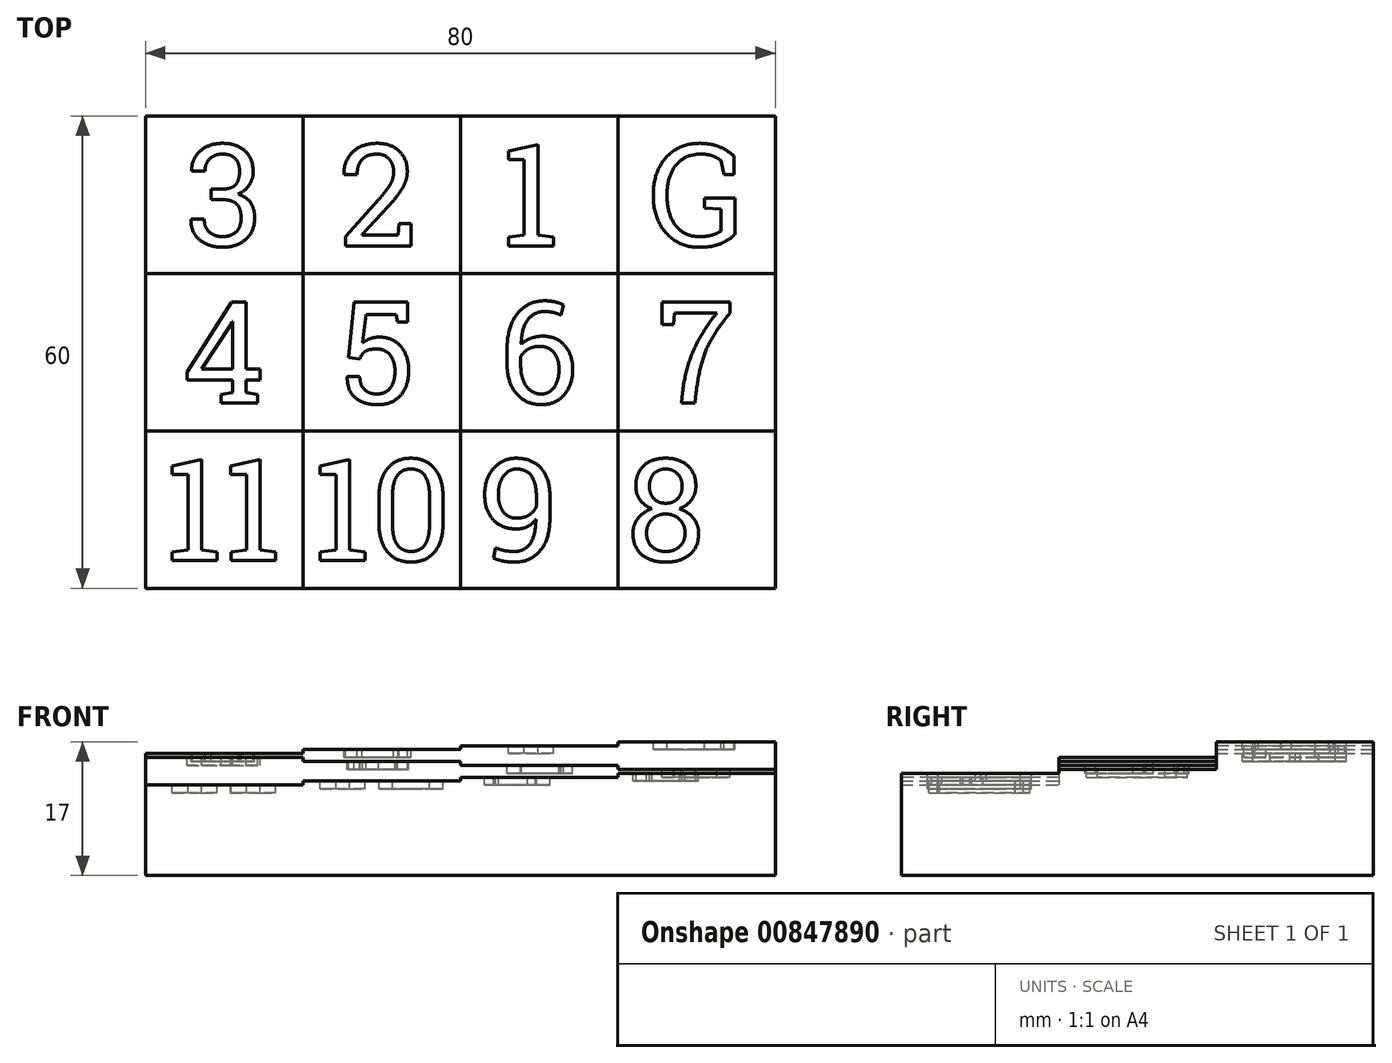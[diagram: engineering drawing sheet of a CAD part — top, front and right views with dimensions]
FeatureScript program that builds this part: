
annotation { "Feature Type Name" : "Feature", "Feature Type Description" : "" }
export const myFeature = defineFeature(function(context is Context, id is Id, definition is map)
    precondition{}
    {
        {
            var Q0;
            Q0=qCreatedBy(makeId("Top.planeOp"),FACE);
            var sketch = newSketch(context, id + "F0", { "sketchPlane" : qUnion([Q0])});
            skLineSegment(sketch, "E0.bottom", {"start": v(0, 0) * mm, "end": v(80, 0) * mm});
            skLineSegment(sketch, "E0.top", {"start": v(0, 60) * mm, "end": v(80, 60) * mm});
            skLineSegment(sketch, "E0.left", {"start": v(0, 0) * mm, "end": v(0, 60) * mm});
            skLineSegment(sketch, "E0.right", {"start": v(80, 0) * mm, "end": v(80, 60) * mm});
            skLineSegment(sketch, "E1", {"start": v(20, 0) * mm, "end": v(20, 60) * mm});
            skLineSegment(sketch, "E2", {"start": v(40, 60) * mm, "end": v(40, 0) * mm});
            skLineSegment(sketch, "E3", {"start": v(60, 60) * mm, "end": v(60, 0) * mm});
            skLineSegment(sketch, "E4", {"start": v(0, 40) * mm, "end": v(80, 40) * mm});
            skLineSegment(sketch, "E5", {"start": v(0, 20) * mm, "end": v(80, 20) * mm});
            skSolve(sketch);
        }
        {
            assignVariable(context, id + "F1", {"variableType" : VariableType.LENGTH, "name" : "H", "lengthValue" : 17 * mm});
        }
        {
            var Q0;
            {var subQ0=sQuery(id+"F0.wireOp",EDGE,"E0.right");var subQ1=sQuery(id+"F0.wireOp",EDGE,"E0.top");var subQ2=makeQuery(id+"F0.imprint","INTERSECT",VERTEX,{"derivedFrom":[subQ1,subQ0]});Q0=makeQuery(id+"F0.imprint","IMPRINT",FACE,{"disambiguationData":[TD([[makeQuery(id+"F0.imprint","IMPRINT",EDGE,{"disambiguationData":[TD([[subQ2,1.0]])],"derivedFrom":subQ1}),-1.0]])]});}
            extrude(context, id + "F2", {"entities" : qUnion([Q0]), "depth" : getVariable(context, 'H'), "offsetDistance" : 25 * mm});
        }
        {
            var Q0;
            {var subQ0=sQuery(id+"F0.wireOp",EDGE,"E2");var subQ1=sQuery(id+"F0.wireOp",EDGE,"E0.top");var subQ2=makeQuery(id+"F0.imprint","INTERSECT",VERTEX,{"derivedFrom":[subQ1,subQ0]});Q0=makeQuery(id+"F0.imprint","IMPRINT",FACE,{"disambiguationData":[TD([[makeQuery(id+"F0.imprint","IMPRINT",EDGE,{"disambiguationData":[TD([[subQ2,-1.0]])],"derivedFrom":subQ1}),-1.0]])]});}
            extrude(context, id + "F3", {"entities" : qUnion([Q0]), "operationType" : NewBodyOperationType.ADD, "depth" : (getVariable(context, 'H')) - 0.5 * mm, "offsetDistance" : 25 * mm});
        }
        {
            var Q0;
            {var subQ0=sQuery(id+"F0.wireOp",EDGE,"E1");var subQ1=sQuery(id+"F0.wireOp",EDGE,"E0.top");var subQ2=makeQuery(id+"F0.imprint","INTERSECT",VERTEX,{"derivedFrom":[subQ1,subQ0]});Q0=makeQuery(id+"F0.imprint","IMPRINT",FACE,{"disambiguationData":[TD([[makeQuery(id+"F0.imprint","IMPRINT",EDGE,{"disambiguationData":[TD([[subQ2,-1.0]])],"derivedFrom":subQ1}),-1.0]])]});}
            extrude(context, id + "F4", {"entities" : qUnion([Q0]), "operationType" : NewBodyOperationType.ADD, "depth" : (getVariable(context, 'H')) - 1 * mm, "offsetDistance" : 25 * mm});
        }
        {
            var Q0;
            {var subQ0=sQuery(id+"F0.wireOp",EDGE,"E0.left");var subQ1=sQuery(id+"F0.wireOp",EDGE,"E0.top");var subQ2=makeQuery(id+"F0.imprint","INTERSECT",VERTEX,{"derivedFrom":[subQ1,subQ0]});Q0=makeQuery(id+"F0.imprint","IMPRINT",FACE,{"disambiguationData":[TD([[makeQuery(id+"F0.imprint","IMPRINT",EDGE,{"disambiguationData":[TD([[subQ2,-1.0]])],"derivedFrom":subQ1}),-1.0]])]});}
            extrude(context, id + "F5", {"entities" : qUnion([Q0]), "operationType" : NewBodyOperationType.ADD, "depth" : (getVariable(context, 'H')) - 1.5 * mm, "offsetDistance" : 25 * mm});
        }
        {
            var Q0;
            {var subQ0=sQuery(id+"F0.wireOp",EDGE,"E4");var subQ1=sQuery(id+"F0.wireOp",EDGE,"E0.left");var subQ2=makeQuery(id+"F0.imprint","INTERSECT",VERTEX,{"derivedFrom":[subQ1,subQ0]});Q0=makeQuery(id+"F0.imprint","IMPRINT",FACE,{"disambiguationData":[TD([[makeQuery(id+"F0.imprint","IMPRINT",EDGE,{"disambiguationData":[TD([[subQ2,1.0]])],"derivedFrom":subQ1}),-1.0]])]});}
            extrude(context, id + "F6", {"entities" : qUnion([Q0]), "operationType" : NewBodyOperationType.ADD, "depth" : (getVariable(context, 'H')) - 2 * mm, "offsetDistance" : 25 * mm});
        }
        {
            var Q0;
            {var subQ0=sQuery(id+"F0.wireOp",EDGE,"E5");var subQ1=sQuery(id+"F0.wireOp",EDGE,"E1");var subQ2=makeQuery(id+"F0.imprint","INTERSECT",VERTEX,{"derivedFrom":[subQ1,subQ0]});Q0=makeQuery(id+"F0.imprint","IMPRINT",FACE,{"disambiguationData":[TD([[makeQuery(id+"F0.imprint","IMPRINT",EDGE,{"disambiguationData":[TD([[subQ2,-1.0]])],"derivedFrom":subQ1}),-1.0]])]});}
            extrude(context, id + "F7", {"entities" : qUnion([Q0]), "operationType" : NewBodyOperationType.ADD, "depth" : (getVariable(context, 'H')) - 2.5 * mm, "offsetDistance" : 25 * mm});
        }
        {
            var Q0;
            {var subQ0=sQuery(id+"F0.wireOp",EDGE,"E4");var subQ1=sQuery(id+"F0.wireOp",EDGE,"E2");var subQ2=makeQuery(id+"F0.imprint","INTERSECT",VERTEX,{"derivedFrom":[subQ1,subQ0]});Q0=makeQuery(id+"F0.imprint","IMPRINT",FACE,{"disambiguationData":[TD([[makeQuery(id+"F0.imprint","IMPRINT",EDGE,{"disambiguationData":[TD([[subQ2,-1.0]])],"derivedFrom":subQ1}),1.0]])]});}
            extrude(context, id + "F8", {"entities" : qUnion([Q0]), "operationType" : NewBodyOperationType.ADD, "depth" : (getVariable(context, 'H')) - 3 * mm, "offsetDistance" : 25 * mm});
        }
        {
            var Q0;
            {var subQ0=sQuery(id+"F0.wireOp",EDGE,"E4");var subQ1=sQuery(id+"F0.wireOp",EDGE,"E0.right");var subQ2=makeQuery(id+"F0.imprint","INTERSECT",VERTEX,{"derivedFrom":[subQ1,subQ0]});Q0=makeQuery(id+"F0.imprint","IMPRINT",FACE,{"disambiguationData":[TD([[makeQuery(id+"F0.imprint","IMPRINT",EDGE,{"disambiguationData":[TD([[subQ2,1.0]])],"derivedFrom":subQ1}),1.0]])]});}
            extrude(context, id + "F9", {"entities" : qUnion([Q0]), "operationType" : NewBodyOperationType.ADD, "depth" : (getVariable(context, 'H')) - 3.5 * mm, "offsetDistance" : 25 * mm});
        }
        {
            var Q0;
            {var subQ0=sQuery(id+"F0.wireOp",EDGE,"E2");var subQ1=sQuery(id+"F0.wireOp",EDGE,"E0.bottom");var subQ2=makeQuery(id+"F0.imprint","INTERSECT",VERTEX,{"derivedFrom":[subQ1,subQ0]});Q0=makeQuery(id+"F0.imprint","IMPRINT",FACE,{"disambiguationData":[TD([[makeQuery(id+"F0.imprint","IMPRINT",EDGE,{"disambiguationData":[TD([[subQ2,-1.0]])],"derivedFrom":subQ1}),1.0]])]});}
            extrude(context, id + "F10", {"entities" : qUnion([Q0]), "operationType" : NewBodyOperationType.ADD, "depth" : (getVariable(context, 'H')) - 4.5 * mm, "offsetDistance" : 25 * mm});
        }
        {
            var Q0;
            {var subQ0=sQuery(id+"F0.wireOp",EDGE,"E0.left");var subQ1=sQuery(id+"F0.wireOp",EDGE,"E0.bottom");var subQ2=makeQuery(id+"F0.imprint","INTERSECT",VERTEX,{"derivedFrom":[subQ1,subQ0]});Q0=makeQuery(id+"F0.imprint","IMPRINT",FACE,{"disambiguationData":[TD([[makeQuery(id+"F0.imprint","IMPRINT",EDGE,{"disambiguationData":[TD([[subQ2,-1.0]])],"derivedFrom":subQ1}),1.0]])]});}
            extrude(context, id + "F11", {"entities" : qUnion([Q0]), "operationType" : NewBodyOperationType.ADD, "depth" : (getVariable(context, 'H')) - 5.5 * mm, "offsetDistance" : 25 * mm});
        }
        {
            var Q0;
            {var subQ0=sQuery(id+"F0.wireOp",EDGE,"E0.right");var subQ1=sQuery(id+"F0.wireOp",EDGE,"E0.bottom");var subQ2=makeQuery(id+"F0.imprint","INTERSECT",VERTEX,{"derivedFrom":[subQ1,subQ0]});Q0=makeQuery(id+"F0.imprint","IMPRINT",FACE,{"disambiguationData":[TD([[makeQuery(id+"F0.imprint","IMPRINT",EDGE,{"disambiguationData":[TD([[subQ2,1.0]])],"derivedFrom":subQ1}),1.0]])]});}
            extrude(context, id + "F12", {"entities" : qUnion([Q0]), "operationType" : NewBodyOperationType.ADD, "depth" : (getVariable(context, 'H')) - 4 * mm, "offsetDistance" : 25 * mm});
        }
        {
            var Q0;
            {var subQ0=sQuery(id+"F0.wireOp",EDGE,"E1");var subQ1=sQuery(id+"F0.wireOp",EDGE,"E0.bottom");var subQ2=makeQuery(id+"F0.imprint","INTERSECT",VERTEX,{"derivedFrom":[subQ1,subQ0]});Q0=makeQuery(id+"F0.imprint","IMPRINT",FACE,{"disambiguationData":[TD([[makeQuery(id+"F0.imprint","IMPRINT",EDGE,{"disambiguationData":[TD([[subQ2,-1.0]])],"derivedFrom":subQ1}),1.0]])]});}
            extrude(context, id + "F13", {"entities" : qUnion([Q0]), "operationType" : NewBodyOperationType.ADD, "depth" : (getVariable(context, 'H')) - 5 * mm, "offsetDistance" : 25 * mm});
        }
        {
            var Q0;
            Q0=makeQuery(id+"F2.opExtrude","CAP_FACE",FACE,{"disambiguationData":[OSD([sQuery(id+"F0.wireOp",EDGE,"E0.top"),sQuery(id+"F0.wireOp",EDGE,"E0.right"),sQuery(id+"F0.wireOp",EDGE,"E3"),sQuery(id+"F0.wireOp",EDGE,"E4")])],"isStart":false});
            var sketch = newSketch(context, id + "F14", { "sketchPlane" : qUnion([Q0])});
            skText(sketch, "E6", { "text": "G", "fontName": "RobotoSlab-Regular.ttf"});
            skLineSegment(sketch, "E7", {"start": v(70, 40) * mm, "end": v(70, 43.5) * mm, "construction": true});
            skLineSegment(sketch, "E8", {"start": v(60, 50) * mm, "end": v(64.02, 50) * mm, "construction": true});
            const initialGuessF14  = {"E6": [0.06402, 0.0435, 1, 0, 0.013]};
            skSetInitialGuess(sketch, initialGuessF14);
            skSolve(sketch);
        }
        {
            var Q0;
            Q0=makeQuery(id+"F14.imprint","IMPRINT",FACE,{"disambiguationData":[TD([[makeQuery(id+"F14.imprint","IMPRINT",EDGE,{"derivedFrom":sQuery(id+"F14.wireOp",EDGE,"E6.sketch_text.stroke-0")}),-1.0]])]});
            extrude(context, id + "F15", {"entities" : qUnion([Q0]), "operationType" : NewBodyOperationType.REMOVE, "oppositeDirection" : true, "depth" : 1 * mm, "offsetDistance" : 25 * mm});
        }
        {
            var Q0;
            Q0=makeQuery(id+"F3.opExtrude","CAP_FACE",FACE,{"disambiguationData":[OSD([sQuery(id+"F0.wireOp",EDGE,"E0.top"),sQuery(id+"F0.wireOp",EDGE,"E2"),sQuery(id+"F0.wireOp",EDGE,"E3"),sQuery(id+"F0.wireOp",EDGE,"E4")])],"isStart":false});
            var sketch = newSketch(context, id + "F16", { "sketchPlane" : qUnion([Q0])});
            skText(sketch, "E9", { "text": "1", "fontName": "RobotoSlab-Regular.ttf"});
            skLineSegment(sketch, "E10", {"start": v(40, 50) * mm, "end": v(46.06, 50) * mm, "construction": true});
            skLineSegment(sketch, "E11", {"start": v(50, 40) * mm, "end": v(50, 43.5) * mm, "construction": true});
            const initialGuessF16  = {"E9": [0.04506, 0.0435, 1, 0, 0.013]};
            skSetInitialGuess(sketch, initialGuessF16);
            skSolve(sketch);
        }
        {
            var Q0;
            Q0 = qSketchRegion(id + "F16", true);
            extrude(context, id + "F17", {"entities" : qUnion([Q0]), "operationType" : NewBodyOperationType.REMOVE, "oppositeDirection" : true, "depth" : 1 * mm, "offsetDistance" : 25 * mm});
        }
        {
            var Q0;
            Q0=makeQuery(id+"F4.opExtrude","CAP_FACE",FACE,{"disambiguationData":[OSD([sQuery(id+"F0.wireOp",EDGE,"E0.top"),sQuery(id+"F0.wireOp",EDGE,"E1"),sQuery(id+"F0.wireOp",EDGE,"E2"),sQuery(id+"F0.wireOp",EDGE,"E4")])],"isStart":false});
            var sketch = newSketch(context, id + "F18", { "sketchPlane" : qUnion([Q0])});
            skText(sketch, "E12", { "text": "2", "fontName": "RobotoSlab-Regular.ttf"});
            skLineSegment(sketch, "E13", {"start": v(20, 50) * mm, "end": v(24.86, 50) * mm, "construction": true});
            skLineSegment(sketch, "E14", {"start": v(30, 43.5) * mm, "end": v(30, 40) * mm, "construction": true});
            const initialGuessF18  = {"E12": [0.02453, 0.0435, 1, 0, 0.013]};
            skSetInitialGuess(sketch, initialGuessF18);
            skSolve(sketch);
        }
        {
            var Q0;
            Q0 = qSketchRegion(id + "F18", true);
            extrude(context, id + "F19", {"entities" : qUnion([Q0]), "operationType" : NewBodyOperationType.REMOVE, "oppositeDirection" : true, "depth" : 1 * mm, "offsetDistance" : 25 * mm});
        }
        {
            var Q0;
            Q0=makeQuery(id+"F5.opExtrude","CAP_FACE",FACE,{"disambiguationData":[OSD([sQuery(id+"F0.wireOp",EDGE,"E0.top"),sQuery(id+"F0.wireOp",EDGE,"E0.left"),sQuery(id+"F0.wireOp",EDGE,"E1"),sQuery(id+"F0.wireOp",EDGE,"E4")])],"isStart":false});
            var sketch = newSketch(context, id + "F20", { "sketchPlane" : qUnion([Q0])});
            skText(sketch, "E15", { "text": "3", "fontName": "RobotoSlab-Regular.ttf"});
            skLineSegment(sketch, "E16", {"start": v(0, 50) * mm, "end": v(5.06, 50) * mm, "construction": true});
            skLineSegment(sketch, "E17", {"start": v(10, 43.5) * mm, "end": v(10, 40) * mm, "construction": true});
            const initialGuessF20  = {"E15": [0.00511, 0.0435, 1, 0, 0.013]};
            skSetInitialGuess(sketch, initialGuessF20);
            skSolve(sketch);
        }
        {
            var Q0;
            Q0 = qSketchRegion(id + "F20", true);
            extrude(context, id + "F21", {"entities" : qUnion([Q0]), "operationType" : NewBodyOperationType.REMOVE, "oppositeDirection" : true, "depth" : 1 * mm, "offsetDistance" : 25 * mm});
        }
        {
            var Q0;
            Q0=makeQuery(id+"F6.opExtrude","CAP_FACE",FACE,{"disambiguationData":[OSD([sQuery(id+"F0.wireOp",EDGE,"E0.left"),sQuery(id+"F0.wireOp",EDGE,"E1"),sQuery(id+"F0.wireOp",EDGE,"E4"),sQuery(id+"F0.wireOp",EDGE,"E5")])],"isStart":false});
            var sketch = newSketch(context, id + "F22", { "sketchPlane" : qUnion([Q0])});
            skText(sketch, "E18", { "text": "4", "fontName": "RobotoSlab-Regular.ttf"});
            skLineSegment(sketch, "E19", {"start": v(0, 30) * mm, "end": v(4.53, 30) * mm, "construction": true});
            skLineSegment(sketch, "E20", {"start": v(10, 23.5) * mm, "end": v(10, 20) * mm, "construction": true});
            const initialGuessF22  = {"E18": [0.00474, 0.0235, 1, 0, 0.013]};
            skSetInitialGuess(sketch, initialGuessF22);
            skSolve(sketch);
        }
        {
            var Q0;
            Q0 = qSketchRegion(id + "F22", true);
            extrude(context, id + "F23", {"entities" : qUnion([Q0]), "operationType" : NewBodyOperationType.REMOVE, "oppositeDirection" : true, "depth" : 1 * mm, "offsetDistance" : 25 * mm});
        }
        {
            var Q0;
            Q0=makeQuery(id+"F7.opExtrude","CAP_FACE",FACE,{"disambiguationData":[OSD([sQuery(id+"F0.wireOp",EDGE,"E1"),sQuery(id+"F0.wireOp",EDGE,"E2"),sQuery(id+"F0.wireOp",EDGE,"E4"),sQuery(id+"F0.wireOp",EDGE,"E5")])],"isStart":false});
            var sketch = newSketch(context, id + "F24", { "sketchPlane" : qUnion([Q0])});
            skText(sketch, "E21", { "text": "5", "fontName": "RobotoSlab-Regular.ttf"});
            skLineSegment(sketch, "E22", {"start": v(40, 30) * mm, "end": v(34.89, 30) * mm, "construction": true});
            skLineSegment(sketch, "E23", {"start": v(30, 23.5) * mm, "end": v(30, 20) * mm, "construction": true});
            const initialGuessF24  = {"E21": [0.02477, 0.0235, 1, 0, 0.013]};
            skSetInitialGuess(sketch, initialGuessF24);
            skSolve(sketch);
        }
        {
            var Q0;
            Q0 = qSketchRegion(id + "F24", true);
            extrude(context, id + "F25", {"entities" : qUnion([Q0]), "operationType" : NewBodyOperationType.REMOVE, "oppositeDirection" : true, "depth" : 1 * mm, "offsetDistance" : 25 * mm});
        }
        {
            var Q0;
            Q0=makeQuery(id+"F8.opExtrude","CAP_FACE",FACE,{"disambiguationData":[OSD([sQuery(id+"F0.wireOp",EDGE,"E2"),sQuery(id+"F0.wireOp",EDGE,"E3"),sQuery(id+"F0.wireOp",EDGE,"E4"),sQuery(id+"F0.wireOp",EDGE,"E5")])],"isStart":false});
            var sketch = newSketch(context, id + "F26", { "sketchPlane" : qUnion([Q0])});
            skText(sketch, "E24", { "text": "6", "fontName": "RobotoSlab-Regular.ttf"});
            skLineSegment(sketch, "E25", {"start": v(55.26, 30) * mm, "end": v(60, 30) * mm, "construction": true});
            skLineSegment(sketch, "E26", {"start": v(50, 23.5) * mm, "end": v(50, 20) * mm, "construction": true});
            const initialGuessF26  = {"E24": [0.04486, 0.0235, 1, 0, 0.013]};
            skSetInitialGuess(sketch, initialGuessF26);
            skSolve(sketch);
        }
        {
            var Q0;
            Q0 = qSketchRegion(id + "F26", true);
            extrude(context, id + "F27", {"entities" : qUnion([Q0]), "operationType" : NewBodyOperationType.REMOVE, "oppositeDirection" : true, "depth" : 1 * mm, "offsetDistance" : 25 * mm});
        }
        {
            var Q0;
            Q0=makeQuery(id+"F9.opExtrude","CAP_FACE",FACE,{"disambiguationData":[OSD([sQuery(id+"F0.wireOp",EDGE,"E0.right"),sQuery(id+"F0.wireOp",EDGE,"E3"),sQuery(id+"F0.wireOp",EDGE,"E4"),sQuery(id+"F0.wireOp",EDGE,"E5")])],"isStart":false});
            var sketch = newSketch(context, id + "F28", { "sketchPlane" : qUnion([Q0])});
            skText(sketch, "E27", { "text": "7", "fontName": "RobotoSlab-Regular.ttf"});
            skLineSegment(sketch, "E28", {"start": v(80, 30) * mm, "end": v(75.23, 30) * mm, "construction": true});
            skLineSegment(sketch, "E29", {"start": v(70, 23.5) * mm, "end": v(70, 20) * mm, "construction": true});
            const initialGuessF28  = {"E27": [0.06492, 0.0235, 1, 0, 0.013]};
            skSetInitialGuess(sketch, initialGuessF28);
            skSolve(sketch);
        }
        {
            var Q0;
            Q0 = qSketchRegion(id + "F28", true);
            extrude(context, id + "F29", {"entities" : qUnion([Q0]), "operationType" : NewBodyOperationType.REMOVE, "oppositeDirection" : true, "depth" : 1 * mm, "offsetDistance" : 25 * mm});
        }
        {
            var Q0;
            Q0=makeQuery(id+"F12.opExtrude","CAP_FACE",FACE,{"disambiguationData":[OSD([sQuery(id+"F0.wireOp",EDGE,"E0.bottom"),sQuery(id+"F0.wireOp",EDGE,"E0.right"),sQuery(id+"F0.wireOp",EDGE,"E3"),sQuery(id+"F0.wireOp",EDGE,"E5")])],"isStart":false});
            var sketch = newSketch(context, id + "F30", { "sketchPlane" : qUnion([Q0])});
            skText(sketch, "E30", { "text": "8", "fontName": "RobotoSlab-Regular.ttf"});
            skLineSegment(sketch, "E31", {"start": v(60, 10) * mm, "end": v(64.86, 10) * mm, "construction": true});
            skLineSegment(sketch, "E32", {"start": v(70, 3.5) * mm, "end": v(70, 0) * mm, "construction": true});
            const initialGuessF30  = {"E30": [0.0611, 0.0035, 1, 0, 0.013]};
            skSetInitialGuess(sketch, initialGuessF30);
            skSolve(sketch);
        }
        {
            var Q0;
            Q0 = qSketchRegion(id + "F30", true);
            extrude(context, id + "F31", {"entities" : qUnion([Q0]), "operationType" : NewBodyOperationType.REMOVE, "oppositeDirection" : true, "depth" : 1 * mm, "offsetDistance" : 25 * mm});
        }
        {
            var Q0;
            Q0=makeQuery(id+"F10.opExtrude","CAP_FACE",FACE,{"disambiguationData":[OSD([sQuery(id+"F0.wireOp",EDGE,"E0.bottom"),sQuery(id+"F0.wireOp",EDGE,"E2"),sQuery(id+"F0.wireOp",EDGE,"E3"),sQuery(id+"F0.wireOp",EDGE,"E5")])],"isStart":false});
            var sketch = newSketch(context, id + "F32", { "sketchPlane" : qUnion([Q0])});
            skText(sketch, "E33", { "text": "9", "fontName": "RobotoSlab-Regular.ttf"});
            skLineSegment(sketch, "E34", {"start": v(40, 10) * mm, "end": v(44.92, 10) * mm, "construction": true});
            skLineSegment(sketch, "E35", {"start": v(50, 0) * mm, "end": v(50, 3.5) * mm, "construction": true});
            const initialGuessF32  = {"E33": [0.04234, 0.0035, 1, 0, 0.013]};
            skSetInitialGuess(sketch, initialGuessF32);
            skSolve(sketch);
        }
        {
            var Q0;
            Q0 = qSketchRegion(id + "F32", true);
            extrude(context, id + "F33", {"entities" : qUnion([Q0]), "operationType" : NewBodyOperationType.REMOVE, "oppositeDirection" : true, "depth" : 1 * mm, "offsetDistance" : 25 * mm});
        }
        {
            var Q0;
            Q0=makeQuery(id+"F13.opExtrude","CAP_FACE",FACE,{"disambiguationData":[OSD([sQuery(id+"F0.wireOp",EDGE,"E0.bottom"),sQuery(id+"F0.wireOp",EDGE,"E1"),sQuery(id+"F0.wireOp",EDGE,"E2"),sQuery(id+"F0.wireOp",EDGE,"E5")])],"isStart":false});
            var sketch = newSketch(context, id + "F34", { "sketchPlane" : qUnion([Q0])});
            skText(sketch, "E36", { "text": "10", "fontName": "RobotoSlab-Regular.ttf"});
            skLineSegment(sketch, "E37", {"start": v(30, 0) * mm, "end": v(30, 3.5) * mm, "construction": true});
            skLineSegment(sketch, "E38", {"start": v(20, 10) * mm, "end": v(21.1, 10) * mm, "construction": true});
            const initialGuessF34  = {"E36": [0.02113, 0.0035, 1, 0, 0.013]};
            skSetInitialGuess(sketch, initialGuessF34);
            skSolve(sketch);
        }
        {
            var Q0;
            Q0 = qSketchRegion(id + "F34", true);
            extrude(context, id + "F35", {"entities" : qUnion([Q0]), "operationType" : NewBodyOperationType.REMOVE, "oppositeDirection" : true, "depth" : 1 * mm, "offsetDistance" : 25 * mm});
        }
        {
            var Q0;
            Q0=makeQuery(id+"F11.opExtrude","CAP_FACE",FACE,{"disambiguationData":[OSD([sQuery(id+"F0.wireOp",EDGE,"E0.bottom"),sQuery(id+"F0.wireOp",EDGE,"E0.left"),sQuery(id+"F0.wireOp",EDGE,"E1"),sQuery(id+"F0.wireOp",EDGE,"E5")])],"isStart":false});
            var sketch = newSketch(context, id + "F36", { "sketchPlane" : qUnion([Q0])});
            skText(sketch, "E39", { "text": "11", "fontName": "RobotoSlab-Regular.ttf"});
            skLineSegment(sketch, "E40", {"start": v(10, 0) * mm, "end": v(10, 3.5) * mm, "construction": true});
            skPoint(sketch, "E40.startSnap0", {"position": v(10, 0) * mm});
            skLineSegment(sketch, "E41", {"start": v(0, 10) * mm, "end": v(2.34, 10) * mm, "construction": true});
            const initialGuessF36  = {"E39": [0.00234, 0.0035, 1, 0, 0.013]};
            skSetInitialGuess(sketch, initialGuessF36);
            skSolve(sketch);
        }
        {
            var Q0;
            Q0 = qSketchRegion(id + "F36", true);
            extrude(context, id + "F37", {"entities" : qUnion([Q0]), "operationType" : NewBodyOperationType.REMOVE, "oppositeDirection" : true, "depth" : 1 * mm, "offsetDistance" : 25 * mm});
        }
    });
